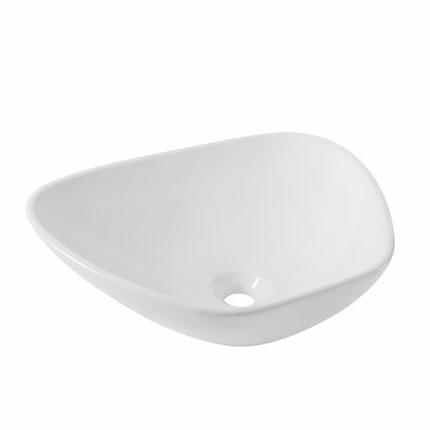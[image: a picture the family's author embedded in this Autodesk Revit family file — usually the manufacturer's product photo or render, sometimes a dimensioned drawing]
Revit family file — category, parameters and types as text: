
# Revit family: LV CLAP
name_source: partatom
category: Plumbing Fixtures
units: mm (PartAtom-declared; Revit-internal decimal feet)

## family parameters
Always vertical = Yes
Cut with Voids When Loaded = No
OmniClass Number = 23.45.00.00
OmniClass Title = Sanitary, Laundry, and Cleaning Equipment
Part Type = Normal
Room Calculation Point = No
Round Connector Dimension = Use Diameter
Shared = No
Work Plane-Based = No

## types (2) — shared parameters
Data Sheet = https://www.helvex.com.mx
Default Elevation = 0"
Features = Perfect Assembly; Uniformity
High Gloss Ceramic = High Gloss Ceramic
Instructive = https://www.helvex.com.mx
Manufacturer = HELVEX
Type Comments = SANIVEX
URL = https://www.helvex.com.mx

## per-type parameters (varying)
| type | Description | Total Height | Total Length | Total Width | Type Image |
| LV CASSINI | Cassini Lavatory to Cap Without Sprill Way | 7" | 17" | 17" | <None> |
| LV CLAP | Clap Lavatory to Cap Without Sprill Way | 6" | 15" | 19" | LV CLAP.jpg |

note: column(s) folded — value = type name in every type: Model

## geometry (parser evidence)
native form markers: Sweep x3
no freeform markers — native parametric forms only
